# Revit family: Lighting-Recessed-Amerlux-E475SA-C3
name_source: partatom
category: Lighting Fixtures
revit_build: Autodesk Revit LT 2014 (Build: 20130308_1515(x64)
units: mm (PartAtom-declared; Revit-internal decimal feet)

## types (2) — shared parameters
Aperture Size = 4 3/4"
Apparent Load = 0 VA
Color Filter = 16777215
Default Elevation = 48"
Description = 4.5" Square Adjustable C3
Dimming Lamp Color Temperature Shift = <None>
Emit Shape Visible in Rendering = No
Emit from Rectangle Length = 4 3/4"
Emit from Rectangle Width = 4 3/4"
Height = 8 1/4"
Lamp = LED
Length = 14 1/2"
Manufacturer = Amerlux
Model = E475SA-C3
Number of Poles = 1
Photometric Web File = generic
Power Factor = 1
Tilt Angle = -90.00°
Trim Size = 5 3/4"
URL = http://www.amerlux.com
Voltage = 0 V
Width = 12 1/2"

## per-type parameters (varying)
| type | Trim |
| Trim | Yes |
| Trimless | No |

## geometry (parser evidence)
native form markers: Blend x10, Sweep x1
no freeform markers — native parametric forms only
